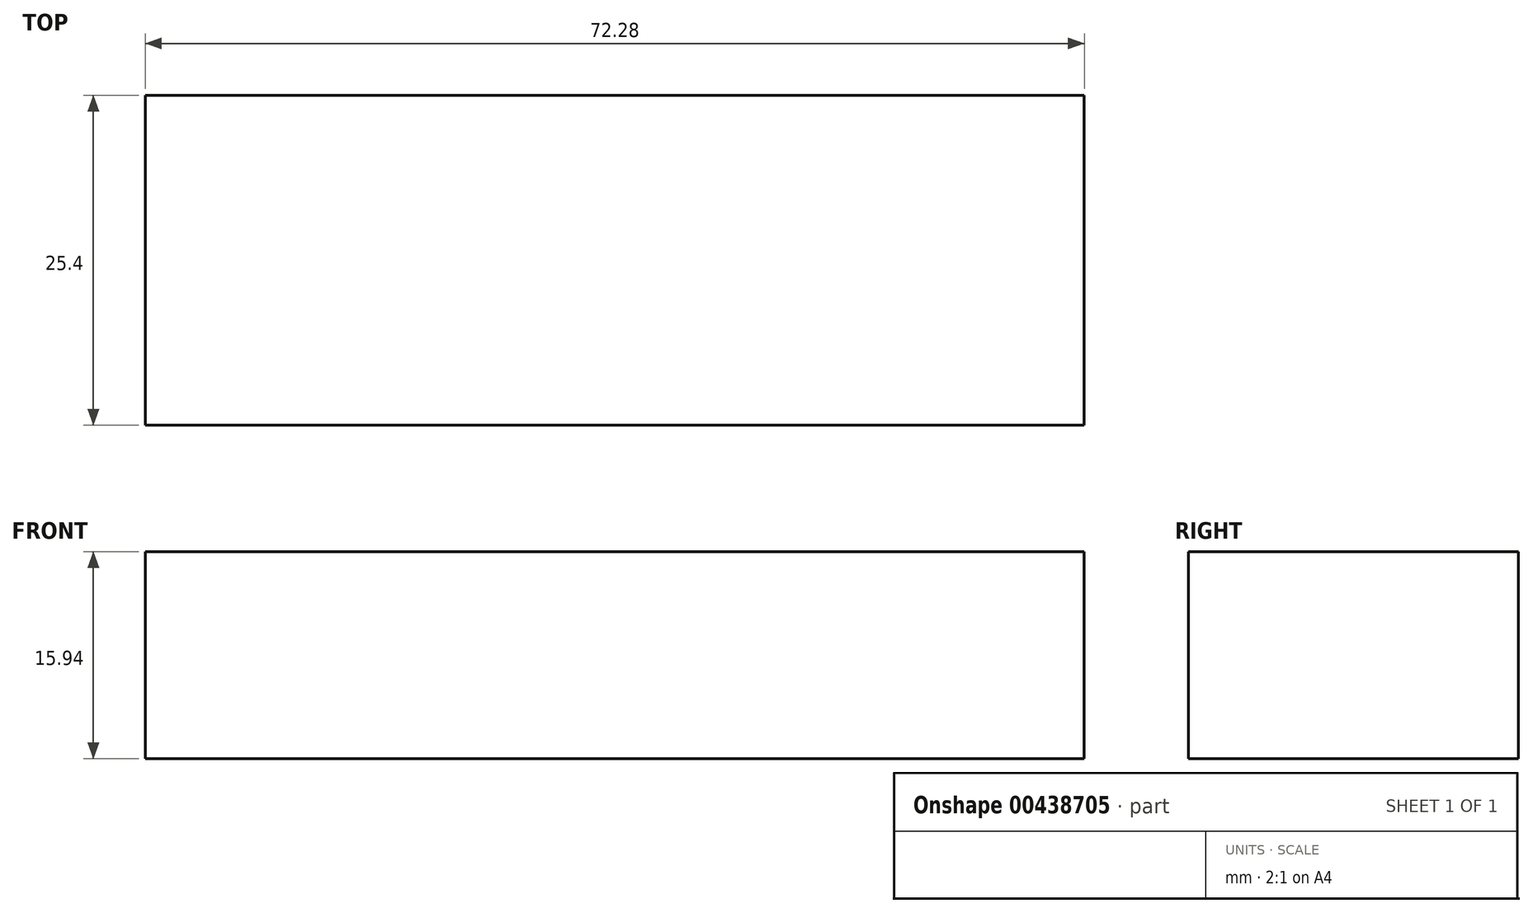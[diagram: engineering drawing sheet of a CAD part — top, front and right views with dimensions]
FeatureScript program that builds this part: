
annotation { "Feature Type Name" : "Feature", "Feature Type Description" : "" }
export const myFeature = defineFeature(function(context is Context, id is Id, definition is map)
    precondition{}
    {
        {
            var Q0;
            Q0=qCreatedBy(makeId("Front.planeOp"),FACE);
            var sketch = newSketch(context, id + "F0", { "sketchPlane" : qUnion([Q0])});
            skLineSegment(sketch, "E0.bottom", {"start": v(-36.14, 7.97) * mm, "end": v(36.14, 7.97) * mm});
            skLineSegment(sketch, "E0.top", {"start": v(-36.14, -7.97) * mm, "end": v(36.14, -7.97) * mm});
            skLineSegment(sketch, "E0.left", {"start": v(-36.14, 7.97) * mm, "end": v(-36.14, -7.97) * mm});
            skLineSegment(sketch, "E0.right", {"start": v(36.14, 7.97) * mm, "end": v(36.14, -7.97) * mm});
            skPoint(sketch, "E0.middle", {"position": v(0, 0) * mm});
            skLineSegment(sketch, "E1.bottom", {"start": v(73.96, 77.23) * mm, "end": v(92.9, 77.23) * mm});
            skLineSegment(sketch, "E1.top", {"start": v(73.96, 61.05) * mm, "end": v(92.9, 61.05) * mm});
            skLineSegment(sketch, "E1.left", {"start": v(73.96, 77.23) * mm, "end": v(73.96, 61.05) * mm});
            skLineSegment(sketch, "E1.right", {"start": v(92.9, 77.23) * mm, "end": v(92.9, 61.05) * mm});
            skLineSegment(sketch, "E2", {"start": v(36.14, 7.97) * mm, "end": v(36.14, 41.91) * mm});
            skArc(sketch, "E3", {"start": v(36.14, 41.91) * mm, "mid": v(42.75, 58.41) * mm, "end": v(58.93, 65.78) * mm});
            skLineSegment(sketch, "E4", {"start": v(58.93, 65.78) * mm, "end": v(79.68, 65.78) * mm});
            skSolve(sketch);
        }
        {
            var Q0;
            Q0=makeQuery(id+"F0.imprint","IMPRINT",FACE,{"disambiguationData":[TD([[makeQuery(id+"F0.imprint","IMPRINT",EDGE,{"derivedFrom":sQuery(id+"F0.wireOp",EDGE,"E0.bottom")}),-1.0]])]});
            extrude(context, id + "F1", {"entities" : qUnion([Q0]), "depth" : 25.4 * mm});
        }
    });
